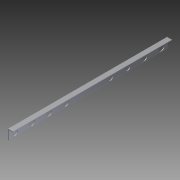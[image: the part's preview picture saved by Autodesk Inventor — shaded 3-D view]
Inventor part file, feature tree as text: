
AUTODESK INVENTOR PART (.ipt)
format: ipt  version: 2012 (Build 160160000, 160)  size: 100,352 bytes
history: native  units: in
note: dims shown in document units (in); Inventor stores cm internally (conversion verified against a paired STEP export)
features: extrude x2, sketch x2
ambient origin geometry x8: Origin, YZ Plane, XZ Plane, XY Plane, X Axis, Y Axis, Z Axis, Center Point
bodies: Solid1 (feature_tree)
feature tree (4):
  extrude  "Extrusion1"  Depth=1.0in
  extrude  "Extrusion2"  Depth=0.125in
  sketch  "Sketch1"  dims[d0=2.0in d1=1.0in]
  sketch  "Sketch2"  dims[d2=0.125in d3=0.125in d4=32.0in d5=0.0in d6=1.125in d7=1.25in d8=0.75in d9=1.125in d10=9.0in d11=1.25in d13=24.25in d14=0.0in d15=10.25in d16=3.4167in d17=3.4167in d18=32.0in d19=3.4167in d20=3.4167in]
